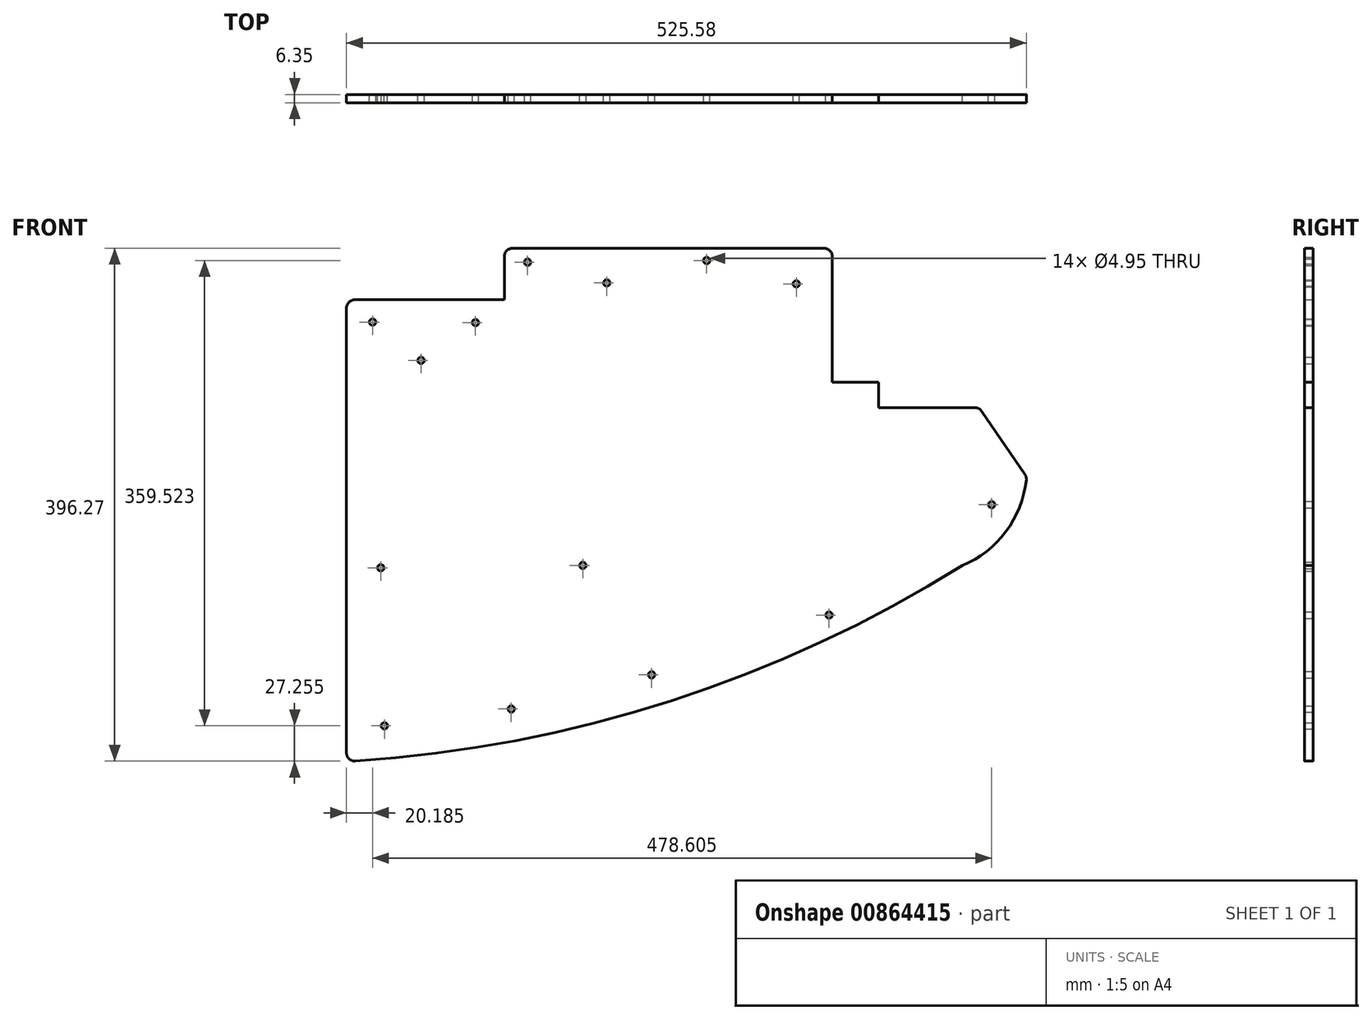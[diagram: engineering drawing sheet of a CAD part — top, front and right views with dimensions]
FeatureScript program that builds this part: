
annotation { "Feature Type Name" : "Feature", "Feature Type Description" : "" }
export const myFeature = defineFeature(function(context is Context, id is Id, definition is map)
    precondition{}
    {
        {
            var Q0;
            Q0=qCreatedBy(makeId("Front.planeOp"),FACE);
            var sketch = newSketch(context, id + "F0", { "sketchPlane" : qUnion([Q0])});
            skLineSegment(sketch, "E0", {"start": v(-72, 8.91) * mm, "end": v(54.98, 6.3) * mm});
            skLineSegment(sketch, "E1", {"start": v(-182.69, -178.1) * mm, "end": v(-182.69, 165.68) * mm});
            skLineSegment(sketch, "E2", {"start": v(-176.34, 172.03) * mm, "end": v(192.85, 172.03) * mm});
            skLineSegment(sketch, "E3", {"start": v(192.85, 172.03) * mm, "end": v(192.85, 108.4) * mm});
            skLineSegment(sketch, "E4", {"start": v(192.85, 108.4) * mm, "end": v(228.53, 108.4) * mm});
            skLineSegment(sketch, "E5", {"start": v(228.53, 108.4) * mm, "end": v(228.53, 88.68) * mm});
            skLineSegment(sketch, "E6", {"start": v(228.53, 88.68) * mm, "end": v(303.11, 88.68) * mm});
            skLineSegment(sketch, "E7", {"start": v(308.35, 85.92) * mm, "end": v(341.78, 37.06) * mm});
            skArc(sketch, "E8", {"start": v(293.32, -33.39) * mm, "mid": v(327.11, -7.06) * mm, "end": v(342.86, 32.78) * mm});
            skArc(sketch, "E9", {"start": v(-175.93, -184.45) * mm, "mid": v(68.06, -138.02) * mm, "end": v(293.32, -33.39) * mm});
            skLineSegment(sketch, "E10", {"start": v(-60.67, 172.03) * mm, "end": v(-60.67, 100.89) * mm});
            skLineSegment(sketch, "E11", {"start": v(-60.67, 172.03) * mm, "end": v(-60.67, 205.46) * mm});
            skLineSegment(sketch, "E12", {"start": v(192.85, 172.03) * mm, "end": v(192.85, 205.46) * mm});
            skLineSegment(sketch, "E13", {"start": v(186.5, 211.81) * mm, "end": v(-54.32, 211.81) * mm});
            skCircle(sketch, "E14", {"center": v(-42.67, 201.05) * mm, "radius": 2.48 * mm});
            skCircle(sketch, "E15", {"center": v(18.52, 185.05) * mm, "radius": 2.48 * mm});
            skCircle(sketch, "E16", {"center": v(95.8, 202.32) * mm, "radius": 2.48 * mm});
            skCircle(sketch, "E17", {"center": v(165.06, 184.35) * mm, "radius": 2.48 * mm});
            skCircle(sketch, "E18", {"center": v(-162.5, 154.82) * mm, "radius": 2.48 * mm});
            skCircle(sketch, "E19", {"center": v(-125.04, 125.16) * mm, "radius": 2.48 * mm});
            skCircle(sketch, "E20", {"center": v(-82.97, 154.37) * mm, "radius": 2.48 * mm});
            skCircle(sketch, "E21", {"center": v(-153.39, -157.2) * mm, "radius": 2.48 * mm});
            skCircle(sketch, "E22", {"center": v(53.19, -117.77) * mm, "radius": 2.48 * mm});
            skCircle(sketch, "E23", {"center": v(316.1, 13.69) * mm, "radius": 2.48 * mm});
            skCircle(sketch, "E24", {"center": v(-156.2, -35.14) * mm, "radius": 2.48 * mm});
            skCircle(sketch, "E25", {"center": v(0, -33.26) * mm, "radius": 2.48 * mm});
            skCircle(sketch, "E26", {"center": v(190.37, -71.6) * mm, "radius": 2.48 * mm});
            skCircle(sketch, "E27", {"center": v(-55.3, -144.25) * mm, "radius": 2.48 * mm});
            skPoint(sketch, "E28.visualSharp", {"position": v(-182.69, -184.86) * mm});
            skArc(sketch, "E28.filletArc", {"start": v(-182.69, -178.1) * mm, "mid": v(-180.68, -182.74) * mm, "end": v(-175.93, -184.45) * mm});
            skPoint(sketch, "E29.visualSharp", {"position": v(306.46, 88.68) * mm});
            skArc(sketch, "E29.filletArc", {"start": v(308.35, 85.92) * mm, "mid": v(306.08, 87.95) * mm, "end": v(303.11, 88.68) * mm});
            skPoint(sketch, "E30.visualSharp", {"position": v(343.08, 35.16) * mm});
            skArc(sketch, "E30.filletArc", {"start": v(342.86, 32.78) * mm, "mid": v(342.7, 35.01) * mm, "end": v(341.78, 37.06) * mm});
            skPoint(sketch, "E31.visualSharp", {"position": v(-182.69, 172.03) * mm});
            skArc(sketch, "E31.filletArc", {"start": v(-176.34, 172.03) * mm, "mid": v(-180.83, 170.17) * mm, "end": v(-182.69, 165.68) * mm});
            skPoint(sketch, "E32.visualSharp", {"position": v(-60.67, 211.81) * mm});
            skArc(sketch, "E32.filletArc", {"start": v(-54.32, 211.81) * mm, "mid": v(-58.81, 209.95) * mm, "end": v(-60.67, 205.46) * mm});
            skPoint(sketch, "E33.visualSharp", {"position": v(192.85, 211.81) * mm});
            skArc(sketch, "E33.filletArc", {"start": v(192.85, 205.46) * mm, "mid": v(190.99, 209.95) * mm, "end": v(186.5, 211.81) * mm});
            skSolve(sketch);
        }
        {
            var Q0;
            Q0 = qSketchRegion(id + "F0", true);
            extrude(context, id + "F1", {"entities" : qUnion([Q0]), "depth" : 6.35 * mm, "offsetDistance" : 25.4 * mm});
        }
    });
